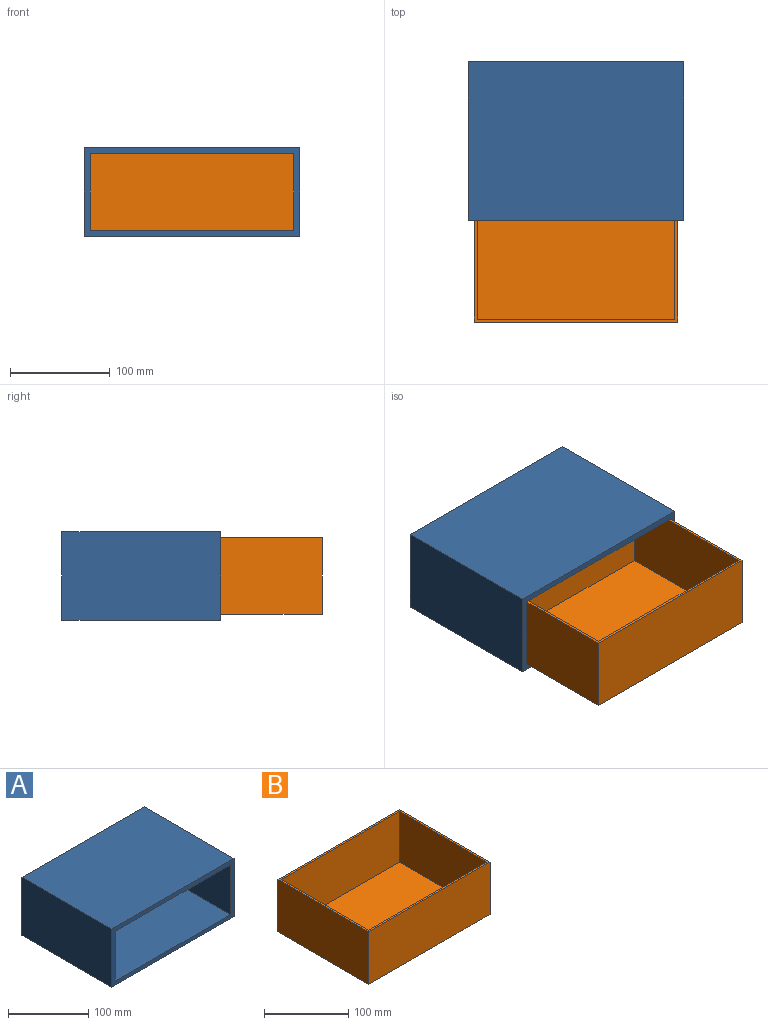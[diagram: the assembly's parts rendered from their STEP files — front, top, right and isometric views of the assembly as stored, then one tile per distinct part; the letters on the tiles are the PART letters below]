
ASSEMBLY  parts=2 mates=1
PART A: 11 faces, bbox 215.9x158.8x88.9 mm
  f0: plane 215.9x158.75mm, normal (0,0,-1), area 34274.1mm2, adj f1,f7,f8,f10
  f1: plane 158.75x88.9mm, normal (1,0,0), area 14112.9mm2, adj f0,f2,f8,f10
  f2: plane 215.9x158.75mm, normal (0,0,1), area 34274.1mm2, adj f1,f7,f8,f10
  f3: plane 203.2x152.4mm, normal (0,0,1), area 30967.7mm2, adj f4,f6,f8,f9
  f4: plane 152.4x76.2mm, normal (1,0,0), area 11612.9mm2, adj f3,f5,f8,f9
  f5: plane 203.2x152.4mm, normal (0,0,-1), area 30967.7mm2, adj f4,f6,f8,f9
  f6: plane 152.4x76.2mm, normal (-1,0,0), area 11612.9mm2, adj f3,f5,f8,f9
  f7: plane 158.75x88.9mm, normal (-1,0,0), area 14112.9mm2, adj f0,f2,f8,f10
  f8: plane 215.9x88.9mm, normal (0,-1,0), area 3709.7mm2, adj f0,f1,f2,f3,f4,f5,f6,f7
  f9: plane 203.2x76.2mm, normal (0,-1,0), area 15483.8mm2, adj f3,f4,f5,f6
  f10: plane 215.9x88.9mm, normal (0,1,0), area 19193.5mm2, adj f0,f1,f2,f7
PART B: 11 faces, bbox 203.2x152.4x76.2 mm
  f0: plane 203.2x152.4mm, normal (0,0,1), area 1780.6mm2, adj f1,f3,f4,f5,f6,f8,f9,f10
  f1: plane 152.4x76.2mm, normal (-1,0,0), area 11612.9mm2, adj f0,f2,f4,f5
  f2: plane 203.2x152.4mm, normal (0,0,-1), area 30967.7mm2, adj f1,f3,f4,f5
  f3: plane 152.4x76.2mm, normal (1,0,0), area 11612.9mm2, adj f0,f2,f4,f5
  f4: plane 203.2x76.2mm, normal (0,1,0), area 15483.8mm2, adj f0,f1,f2,f3
  f5: plane 203.2x76.2mm, normal (0,-1,0), area 15483.8mm2, adj f0,f1,f2,f3
  f6: plane 147.32x73.66mm, normal (1,0,0), area 10851.6mm2, adj f0,f7,f9,f10
  f7: plane 198.12x147.32mm, normal (0,0,1), area 29187mm2, adj f6,f8,f9,f10
  f8: plane 147.32x73.66mm, normal (-1,0,0), area 10851.6mm2, adj f0,f7,f9,f10
  f9: plane 198.12x73.66mm, normal (0,-1,0), area 14593.5mm2, adj f0,f6,f7,f8
  f10: plane 198.12x73.66mm, normal (0,1,0), area 14593.5mm2, adj f0,f6,f7,f8
PLACE A at identity fixed
PLACE B t=(0,-101.6,0)mm
MATE slider B.f4 <-> A.f9  axis (0,1,0) through (203.2,50.8,0)mm
